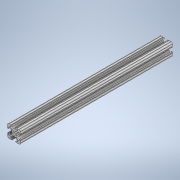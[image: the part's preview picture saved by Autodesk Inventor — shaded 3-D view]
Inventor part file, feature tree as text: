
AUTODESK INVENTOR PART (.ipt)
format: ipt  version: 2020 (Build 240168000, 168)  size: 235,008 bytes
history: native  units: in
note: dims shown in document units (in); Inventor stores cm internally (conversion verified against a paired STEP export)
features: extrude x1, sketch x1
ambient origin geometry x8: Origin, YZ Plane, XZ Plane, XY Plane, X Axis, Y Axis, Z Axis, Center Point
bodies: Solid1 (feature_tree)
feature tree (2):
  extrude  "Extrusion1"  [1 undecoded]
  sketch  "Sketch1"  dims[d0=12.0in d1=0.0in]
note: 1 required parameter value undecoded (feature->parameter linkage not recoverable at this tier; creation-order binding heuristic only, values carry confidence <= 0.55)
